# Revit family: Medical_All_Hill-Rom_TruSystem-7500
name_source: partatom
category: Specialty Equipment
revit_build: Autodesk Revit Architecture 2015 (Build: 20140606_1530(x64)
units: mm (PartAtom-declared; Revit-internal decimal feet)

## types (1)
- TruSystem 7500 Surgical Table
    Apparent Load = 0 VA
    BIMobject category = All
    BIMobject category code = medical-all
    BIMobject main category = Medical
    BIMobject main category code = medical
    Brand url = https://construction.hill-rom.com
    Cap Material = Plastic-Hill-Rom-Black
    Default Elevation = 4' - 0"
    Description = The latest generation of the TruSystem® 7500 OR System Table has larger adjustment areas of the OR tabletops which allow for more flexibility in patient positioning. The overload protection and sensor-controlled collision recognition and avoidance options help to increase patient safety.
    Design country = United States
    Edition number = 1
    Frequency = 50 Hz
    Frequency Range = 50-60 Hz
    Full Load Current = 20 A
    Height Adjustment Max. = 3' - 9"
    Height Adjustment Min. = 1' - 11"
    Height Adjustment Range = 1' - 9 11/16"
    Installation instructions = https://construction.hill-rom.com
    Length = 3' - 6 3/32"
    Lift Material = Leather-Hill-Rom-Black
    Longitudinal Slide = 1' - 3 11/16"
    Manufacturer = Hill-Rom
    Manufacturer country = United States
    Manufacturer name = Hill-Rom
    Model = TruSystem® 7500 Surgical Table
    Nominal height = 0' - 0"
    Nominal width = 0' - 0"
    Nuts Material = Plastic-Hill-Rom-Light Blue
    Patient Weight Capacity = 793.00 lbf
    Power Consumption (max) = 700 W
    Power Factor = 1
    Power Supply = 700 VA
    Product Guid = 60e5de46-e3f4-4c59-bbed-8992c5a8bcfe
    Product SKU = Trumpf-TruSystem7500
    Product data url = https://bimobject.com
    Product family = OR Tables
    Product group = TruSystem7500
    Product url = https://www.trumpfmedical.com
    QR code = http://bimobject.com
    Rail Material = Steel-Hill-Rom-Stainless
    Rotation = 360.00°
    Running Gear Material = Steel-Hill-Rom-Stainless
    Support Material = Steel-Hill-Rom-Stainless
    Table Top Material = Fabric-Hill-Rom-Black
    Technical description = https://construction.hill-rom.com
    Tilting = 45.00°
    Trendelenburg / Reverse Trendelenburg = 20.00°
    URL = https://www.hill-rom.com
    Voltage = 240 V
    Voltage Range = 100-240 V
    Width = 1' - 11 19/32"
    Youtube clip = https://www.youtube.com

## geometry (parser evidence)
native form markers: Blend x6, Sweep x2
no freeform markers — native parametric forms only
